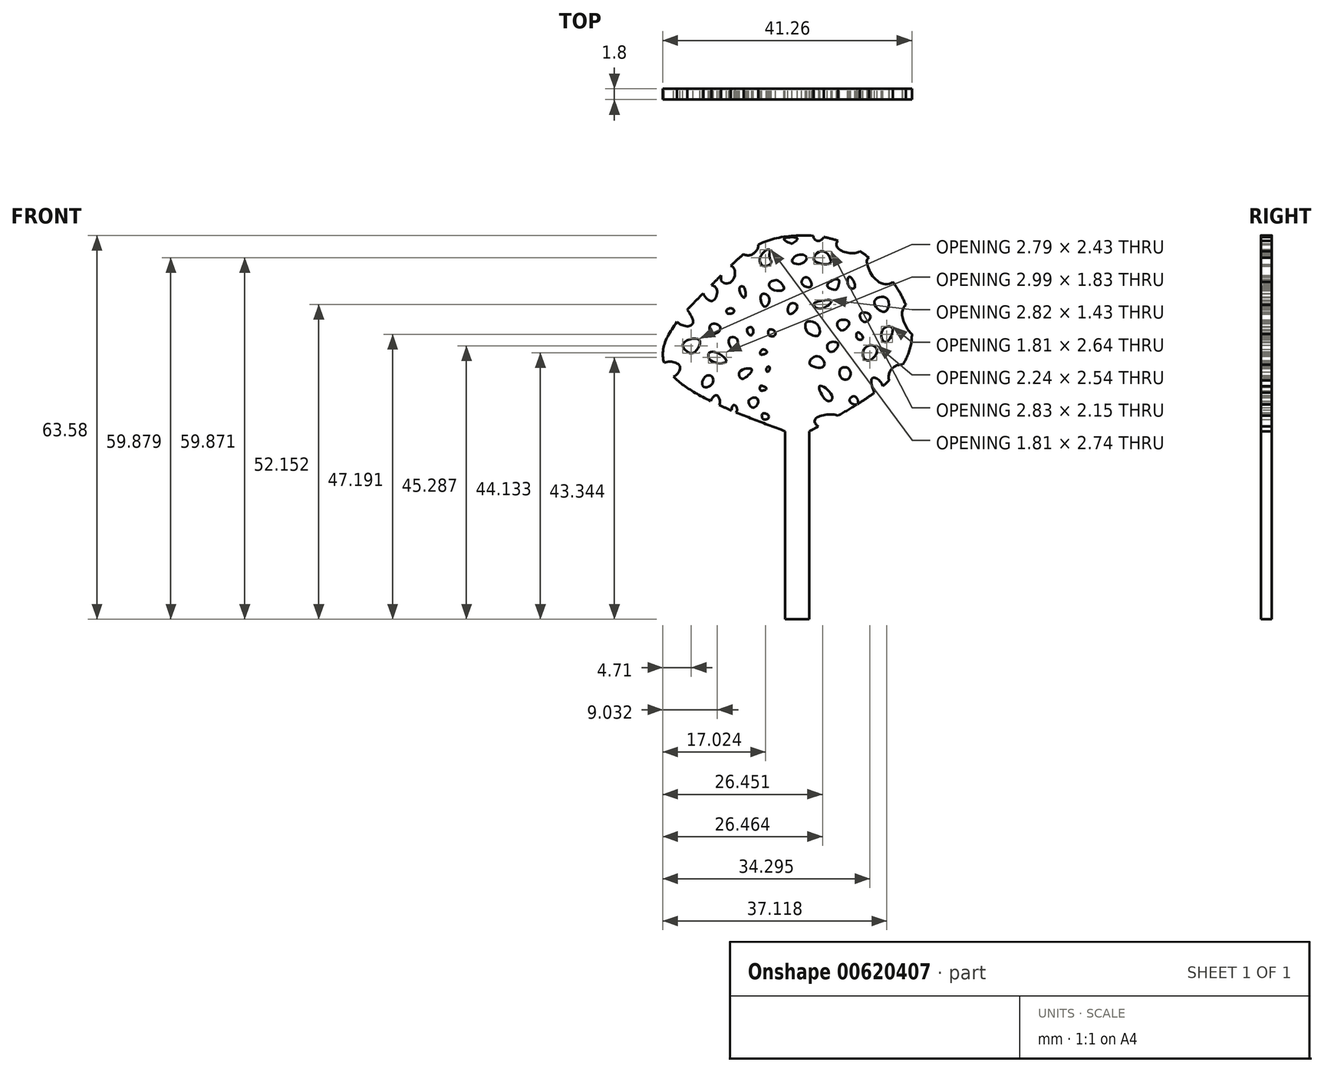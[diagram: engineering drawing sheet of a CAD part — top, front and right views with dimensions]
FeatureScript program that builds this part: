
annotation { "Feature Type Name" : "Feature", "Feature Type Description" : "" }
export const myFeature = defineFeature(function(context is Context, id is Id, definition is map)
    precondition{}
    {
        {
            var Q0;
            Q0=qCreatedBy(makeId("Front.planeOp"),FACE);
            var sketch = newSketch(context, id + "F0", { "sketchPlane" : qUnion([Q0])});
            skLineSegment(sketch, "E0.bottom", {"start": v(-2, 18) * mm, "end": v(2, 18) * mm});
            skLineSegment(sketch, "E0.top", {"start": v(-2, -18) * mm, "end": v(2, -18) * mm});
            skLineSegment(sketch, "E0.left", {"start": v(-2, 18) * mm, "end": v(-2, -18) * mm});
            skLineSegment(sketch, "E0.right", {"start": v(2, 18) * mm, "end": v(2, -18) * mm});
            skPoint(sketch, "E0.middle", {"position": v(0, 0) * mm});
            skLineSegment(sketch, "E1", {"start": v(0, 18) * mm, "end": v(0, 28) * mm});
            skPoint(sketch, "E1.endSnap0", {"position": v(0, 18) * mm});
            skFitSpline(sketch, "E2", {"points": [v(-2, 13.13) * mm, v(-22.24, 25.27) * mm, v(-14.23, 37.34) * mm, v(-6.72, 43.93) * mm, v(0, 45.55) * mm, v(7.68, 44.33) * mm, v(16.4, 37.03) * mm, v(18.22, 25.57) * mm, v(2, 13.13) * mm], "startDerivative": vector(-171.98, 63.77) * mm, "endDerivative": vector(-133.37, -71.47) * mm});
            skFitSpline(sketch, "E3", {"points": [v(-22.75, 22.63) * mm, v(-22.04, 24.48) * mm, v(-19.5, 23.95) * mm, v(-20.52, 22.18) * mm, v(-22.75, 22.63) * mm]});
            skFitSpline(sketch, "E4", {"points": [v(-19.92, 31.24) * mm, v(-20.52, 34.8) * mm, v(-17.27, 31.15) * mm, v(-19.92, 31.24) * mm]});
            skFitSpline(sketch, "E5", {"points": [v(-16.97, 26.28) * mm, v(-16.26, 28.31) * mm, v(-18.9, 27.7) * mm, v(-18.18, 26.28) * mm, v(-16.97, 26.28) * mm]});
            skFitSpline(sketch, "E6", {"points": [v(-15.65, 20.6) * mm, v(-15.24, 22.18) * mm, v(-14.13, 22.18) * mm, v(-14.23, 20.8) * mm, v(-15.65, 20.6) * mm]});
            skFitSpline(sketch, "E7", {"points": [v(-14.35, 18.13) * mm, v(-13.32, 19.08) * mm, v(-12.95, 17.48) * mm, v(-14.23, 16.95) * mm, v(-14.35, 18.13) * mm]});
            skFitSpline(sketch, "E8", {"points": [v(-14.35, 24.86) * mm, v(-14.35, 26.28) * mm, v(-11.76, 24.76) * mm, v(-14.35, 24.86) * mm]});
            skFitSpline(sketch, "E9", {"points": [v(-14.23, 34.7) * mm, v(-15.65, 36.5) * mm, v(-14.23, 37.34) * mm, v(-13.29, 36.28) * mm, v(-14.23, 34.7) * mm]});
            skFitSpline(sketch, "E10", {"points": [v(-14.23, 29.4) * mm, v(-14.35, 30.79) * mm, v(-12.95, 30.63) * mm, v(-12.95, 29.7) * mm, v(-14.23, 29.4) * mm]});
            skFitSpline(sketch, "E11", {"points": [v(-10.5, 26.69) * mm, v(-11.3, 28.45) * mm, v(-9.98, 28.38) * mm, v(-10.5, 26.69) * mm]});
            skFitSpline(sketch, "E12", {"points": [v(-10.9, 16.57) * mm, v(-10.5, 17.48) * mm, v(-9.98, 16.75) * mm, v(-10.5, 15.98) * mm, v(-10.9, 16.57) * mm]});
            skFitSpline(sketch, "E13", {"points": [v(-9.28, 21.89) * mm, v(-9.52, 23) * mm, v(-7.59, 23.4) * mm, v(-8.4, 22.18) * mm, v(-9.28, 21.89) * mm]});
            skFitSpline(sketch, "E14", {"points": [v(-7.34, 17.04) * mm, v(-8.07, 18.13) * mm, v(-6.92, 18.68) * mm, v(-6.5, 17.92) * mm, v(-7.34, 17.04) * mm]});
            skFitSpline(sketch, "E15", {"points": [v(-5.65, 15.16) * mm, v(-5.77, 16.01) * mm, v(-4.89, 15.9) * mm, v(-4.8, 15.29) * mm, v(-5.65, 15.16) * mm]});
            skFitSpline(sketch, "E16", {"points": [v(-6.1, 19.89) * mm, v(-6.13, 20.6) * mm, v(-5.65, 20.6) * mm, v(-5.1, 20.2) * mm, v(-5.65, 19.89) * mm, v(-6.1, 19.89) * mm]});
            skFitSpline(sketch, "E17", {"points": [v(-6.1, 25.89) * mm, v(-6.1, 26.28) * mm, v(-5.65, 26.69) * mm, v(-5.04, 26.28) * mm, v(-5.34, 25.95) * mm, v(-6.1, 25.89) * mm]});
            skFitSpline(sketch, "E18", {"points": [v(-4.92, 22.98) * mm, v(-5.16, 23.4) * mm, v(-4.74, 23.86) * mm, v(-4.56, 23.52) * mm, v(-4.92, 22.98) * mm]});
            skFitSpline(sketch, "E19", {"points": [v(-4.63, 29.01) * mm, v(-4.7, 29.91) * mm, v(-3.8, 29.76) * mm, v(-3.73, 29.01) * mm, v(-4.63, 29.01) * mm]});
            skFitSpline(sketch, "E20", {"points": [v(-7.68, 29.01) * mm, v(-8.32, 30.06) * mm, v(-7.42, 30.22) * mm, v(-7.68, 29.01) * mm]});
            skFitSpline(sketch, "E21", {"points": [v(-11.48, 32.62) * mm, v(-11.76, 33.07) * mm, v(-10.9, 33.53) * mm, v(-10.5, 32.89) * mm, v(-11.48, 32.62) * mm]});
            skFitSpline(sketch, "E22", {"points": [v(-1.3, 32.6) * mm, v(-1.16, 34.25) * mm, v(0, 33.8) * mm, v(-1.3, 32.6) * mm]});
            skFitSpline(sketch, "E23", {"points": [v(-5.37, 33.76) * mm, v(-6.1, 35.15) * mm, v(-5.65, 35.9) * mm, v(-4.63, 35.12) * mm, v(-5.37, 33.76) * mm]});
            skFitSpline(sketch, "E24", {"points": [v(-8.8, 35.27) * mm, v(-8.83, 36.96) * mm, v(-9.58, 36.88) * mm, v(-8.8, 35.27) * mm]});
            skFitSpline(sketch, "E25", {"points": [v(-10.5, 40.12) * mm, v(-11.76, 40.38) * mm, v(-12.56, 38.01) * mm, v(-10.9, 37.94) * mm, v(-10.5, 40.12) * mm]});
            skFitSpline(sketch, "E26", {"points": [v(-7.85, 42.3) * mm, v(-9.58, 43.28) * mm, v(-8.08, 44.86) * mm, v(-6.46, 44.07) * mm, v(-7.85, 42.3) * mm]});
            skFitSpline(sketch, "E27", {"points": [v(-4.63, 43.24) * mm, v(-6.1, 42.08) * mm, v(-5.65, 40.53) * mm, v(-4.32, 41.02) * mm, v(-4.63, 42.08) * mm, v(-4.63, 43.24) * mm]});
            skFitSpline(sketch, "E28", {"points": [v(-2.96, 37.94) * mm, v(-3.57, 38.16) * mm, v(-4.63, 37.67) * mm, v(-4.02, 36.58) * mm, v(-2.21, 36.73) * mm, v(-2.96, 37.94) * mm]});
            skFitSpline(sketch, "E29", {"points": [v(0.5, 40.87) * mm, v(-0.86, 41.29) * mm, v(0.27, 42.38) * mm, v(1.55, 41.89) * mm, v(0.5, 40.87) * mm]});
            skFitSpline(sketch, "E30", {"points": [v(-1.08, 44.26) * mm, v(-2.21, 45) * mm, v(0, 45.09) * mm, v(-0.7, 44.33) * mm, v(-1.08, 44.26) * mm]});
            skFitSpline(sketch, "E31", {"points": [v(4.25, 42.95) * mm, v(2.74, 41.89) * mm, v(3.26, 41.1) * mm, v(5.52, 41.1) * mm, v(4.25, 42.95) * mm]});
            skFitSpline(sketch, "E32", {"points": [v(6.92, 43.3) * mm, v(6.72, 44.7) * mm, v(10.22, 44.58) * mm, v(10.36, 42.93) * mm, v(6.92, 43.3) * mm]});
            skFitSpline(sketch, "E33", {"points": [v(3.32, 44.7) * mm, v(2.68, 45.52) * mm, v(4.13, 46.08) * mm, v(4.37, 45.3) * mm, v(3.32, 44.7) * mm]});
            skFitSpline(sketch, "E34", {"points": [v(6.22, 36.57) * mm, v(4.94, 37.34) * mm, v(6.72, 38.31) * mm, v(6.72, 37.03) * mm, v(6.22, 36.57) * mm]});
            skFitSpline(sketch, "E35", {"points": [v(1.55, 37.03) * mm, v(0.7, 37.85) * mm, v(1.55, 38.66) * mm, v(2.33, 37.34) * mm, v(1.55, 37.03) * mm]});
            skFitSpline(sketch, "E36", {"points": [v(3.73, 33.44) * mm, v(2.74, 34.13) * mm, v(3.67, 34.7) * mm, v(5.64, 34.7) * mm, v(3.73, 33.44) * mm]});
            skFitSpline(sketch, "E37", {"points": [v(2.62, 29.01) * mm, v(1.55, 29.73) * mm, v(1.55, 31.24) * mm, v(3.44, 30.65) * mm, v(3.5, 29.01) * mm, v(2.62, 29.01) * mm]});
            skFitSpline(sketch, "E38", {"points": [v(2.04, 24.33) * mm, v(3.44, 25.55) * mm, v(4.36, 23.92) * mm, v(2.04, 24.33) * mm]});
            skFitSpline(sketch, "E39", {"points": [v(11.56, 40.86) * mm, v(13.07, 38.2) * mm, v(15.83, 37.85) * mm, v(16.4, 41.89) * mm, v(11.86, 41.89) * mm, v(11.56, 40.86) * mm]});
            skFitSpline(sketch, "E40", {"points": [v(9.53, 37.03) * mm, v(8.6, 38.72) * mm, v(8.6, 37.03) * mm, v(9.53, 37.03) * mm]});
            skFitSpline(sketch, "E41", {"points": [v(12.08, 32.28) * mm, v(10.46, 32.63) * mm, v(11.1, 31.24) * mm, v(12.08, 32.28) * mm]});
            skFitSpline(sketch, "E42", {"points": [v(14.63, 35.3) * mm, v(12.78, 34.7) * mm, v(14, 32.97) * mm, v(15.04, 33.55) * mm, v(14.63, 35.3) * mm]});
            skFitSpline(sketch, "E43", {"points": [v(7.38, 29.84) * mm, v(6.72, 31.24) * mm, v(8.54, 31.24) * mm, v(7.38, 29.84) * mm]});
            skFitSpline(sketch, "E44", {"points": [v(5.58, 26.28) * mm, v(5.06, 27.58) * mm, v(6.72, 27.64) * mm, v(5.58, 26.28) * mm]});
            skFitSpline(sketch, "E45", {"points": [v(5.06, 18.13) * mm, v(3.67, 20.6) * mm, v(5.76, 18.93) * mm, v(5.06, 18.13) * mm]});
            skFitSpline(sketch, "E46", {"points": [v(3.9, 13.71) * mm, v(2.97, 15.16) * mm, v(6.72, 15.7) * mm, v(6.72, 14.64) * mm, v(3.9, 13.71) * mm]});
            skFitSpline(sketch, "E47", {"points": [v(8.66, 18.13) * mm, v(9.47, 18.93) * mm, v(9.97, 17.63) * mm, v(8.66, 18.13) * mm]});
            skFitSpline(sketch, "E48", {"points": [v(7.38, 21.89) * mm, v(7.15, 23.46) * mm, v(8.54, 23.46) * mm, v(8.54, 21.89) * mm, v(7.38, 21.89) * mm]});
            skFitSpline(sketch, "E49", {"points": [v(11.56, 24.86) * mm, v(10.86, 26.28) * mm, v(12.31, 27.4) * mm, v(13.18, 26.28) * mm, v(11.56, 24.86) * mm]});
            skFitSpline(sketch, "E50", {"points": [v(9.97, 28.45) * mm, v(9.97, 29.5) * mm, v(10.86, 28.56) * mm, v(9.97, 28.45) * mm]});
            skFitSpline(sketch, "E51", {"points": [v(15.73, 30.19) * mm, v(14.11, 29.96) * mm, v(14.57, 27.87) * mm, v(15.73, 30.19) * mm]});
            skFitSpline(sketch, "E52", {"points": [v(19.04, 34.13) * mm, v(17.36, 32.74) * mm, v(19.68, 29.01) * mm, v(19.04, 34.13) * mm]});
            skFitSpline(sketch, "E53", {"points": [v(18.29, 23.7) * mm, v(15.73, 23.58) * mm, v(15.62, 21.14) * mm, v(18.29, 23.7) * mm]});
            skFitSpline(sketch, "E54", {"points": [v(12.37, 21.89) * mm, v(13.41, 18.82) * mm, v(14.15, 20.6) * mm, v(12.37, 21.89) * mm]});
            skSolve(sketch);
        }
        {
            var Q0;
            Q0=makeQuery(id+"F0.imprint","IMPRINT",FACE,{"disambiguationData":[TD([[makeQuery(id+"F0.imprint","IMPRINT",EDGE,{"derivedFrom":sQuery(id+"F0.wireOp",EDGE,"E5")}),-1.0]])]});
            var Q1;
            {var subQ5=sQuery(id+"F0.wireOp",EDGE,"E0.top");Q1=makeQuery(id+"F0.imprint","IMPRINT",FACE,{"disambiguationData":[TD([[makeQuery(id+"F0.imprint","IMPRINT",EDGE,{"derivedFrom":subQ5}),1.0]])]});}
            extrude(context, id + "F1", {"entities" : qUnion([Q0, Q1]), "depth" : 1.8 * mm, "offsetDistance" : 25 * mm});
        }
    });
